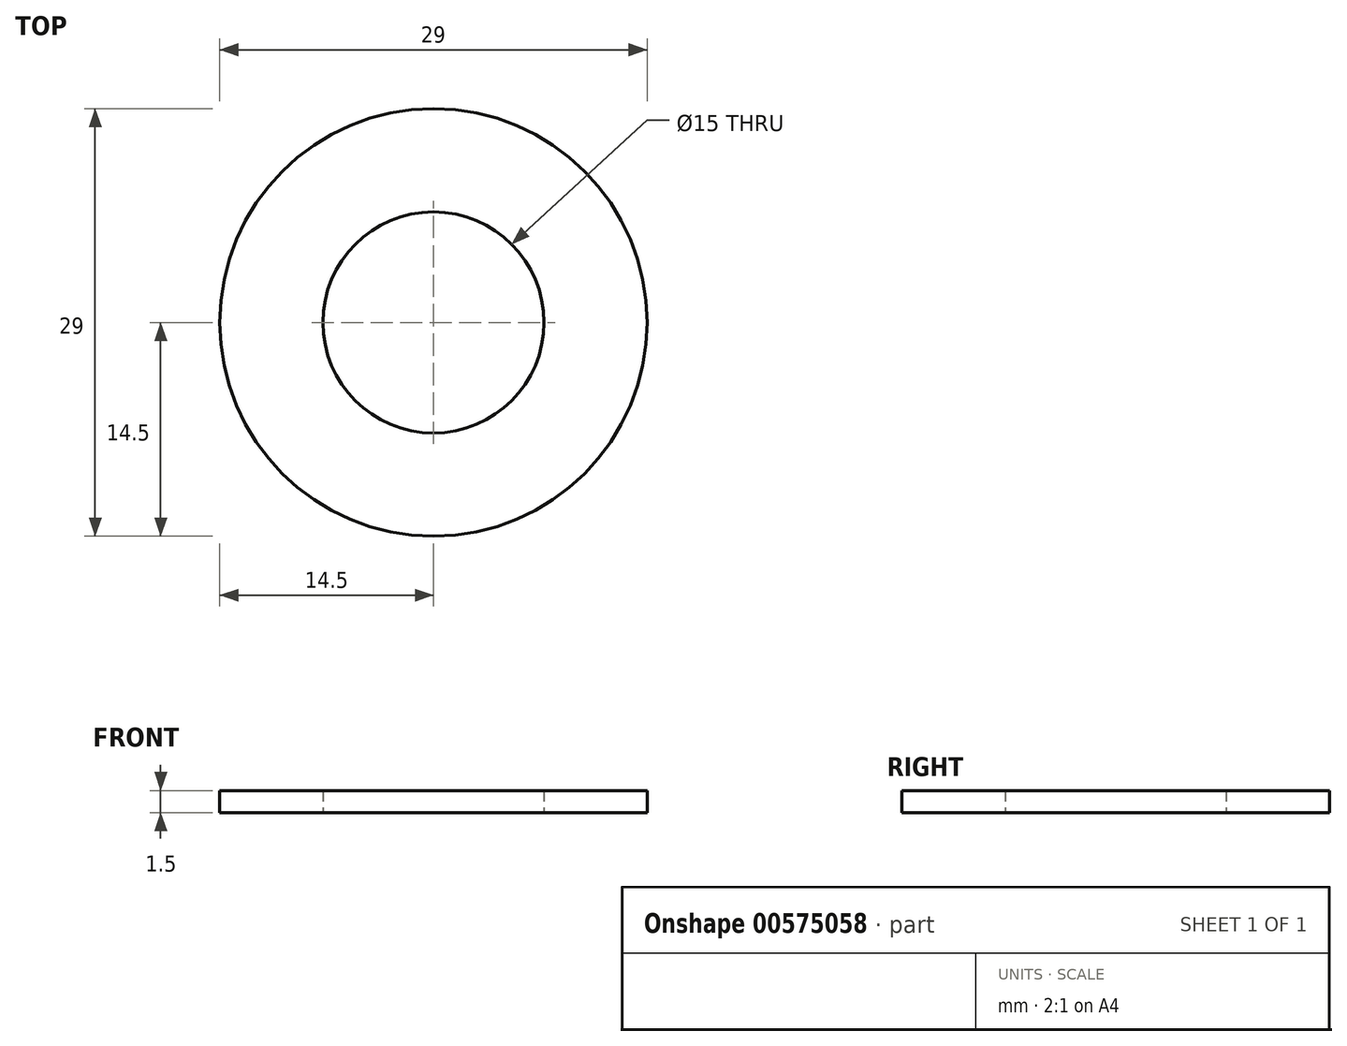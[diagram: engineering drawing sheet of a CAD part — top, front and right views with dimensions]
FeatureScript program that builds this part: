
annotation { "Feature Type Name" : "Feature", "Feature Type Description" : "" }
export const myFeature = defineFeature(function(context is Context, id is Id, definition is map)
    precondition{}
    {
        {
            var Q0;
            Q0=qCreatedBy(makeId("Top.planeOp"),FACE);
            var sketch = newSketch(context, id + "F0", { "sketchPlane" : qUnion([Q0])});
            skCircle(sketch, "E0", {"center": v(0, 0) * mm, "radius": 7.5 * mm});
            skCircle(sketch, "E1.0", {"center": v(0, 0) * mm, "radius": 14.5 * mm});
            skSolve(sketch);
        }
        {
            var Q0;
            Q0=makeQuery(id+"F0.imprint","IMPRINT",FACE,{"disambiguationData":[TD([[makeQuery(id+"F0.imprint","IMPRINT",EDGE,{"derivedFrom":sQuery(id+"F0.wireOp",EDGE,"E0")}),-1.0]])]});
            extrude(context, id + "F1", {"entities" : qUnion([Q0]), "depth" : 1.5 * mm, "offsetDistance" : 25 * mm});
        }
    });
